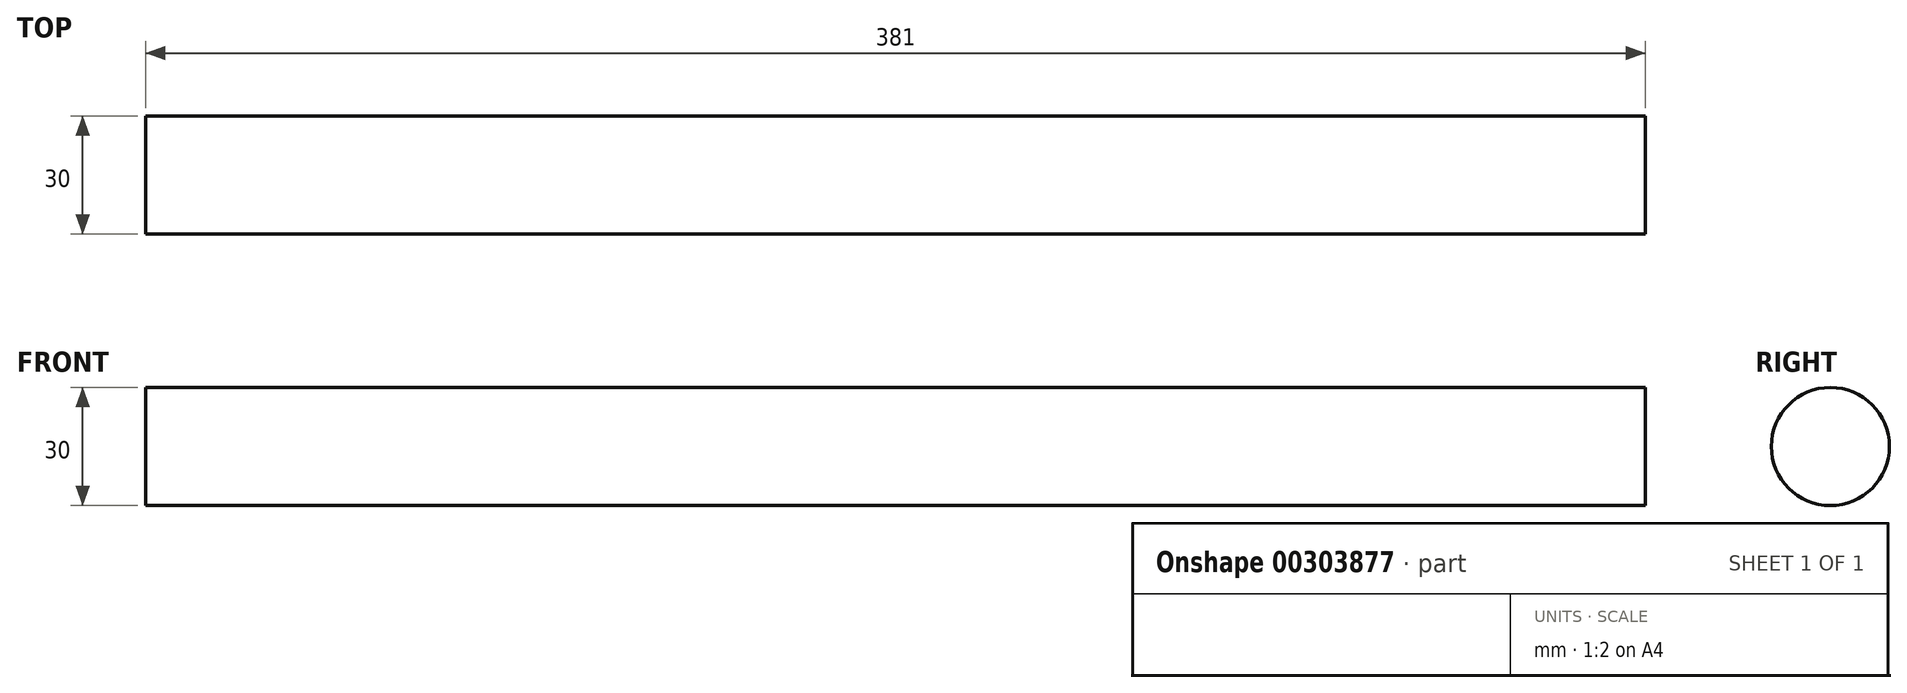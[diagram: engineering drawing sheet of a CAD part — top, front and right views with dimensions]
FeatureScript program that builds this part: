
annotation { "Feature Type Name" : "Feature", "Feature Type Description" : "" }
export const myFeature = defineFeature(function(context is Context, id is Id, definition is map)
    precondition{}
    {
        {
            var Q0;
            Q0=qCreatedBy(makeId("Right.planeOp"),FACE);
            var sketch = newSketch(context, id + "F0", { "sketchPlane" : qUnion([Q0])});
            skCircle(sketch, "E0", {"center": v(0, 0) * mm, "radius": 15 * mm});
            skSolve(sketch);
        }
        {
            var Q0;
            Q0=makeQuery(id+"F0.imprint","IMPRINT",FACE,{"disambiguationData":[TD([[makeQuery(id+"F0.imprint","IMPRINT",EDGE,{"derivedFrom":sQuery(id+"F0.wireOp",EDGE,"E0")}),1.0]])]});
            extrude(context, id + "F1", {"entities" : qUnion([Q0]), "endBound" : BoundingType.SYMMETRIC, "depth" : 381 * mm});
        }
    });
